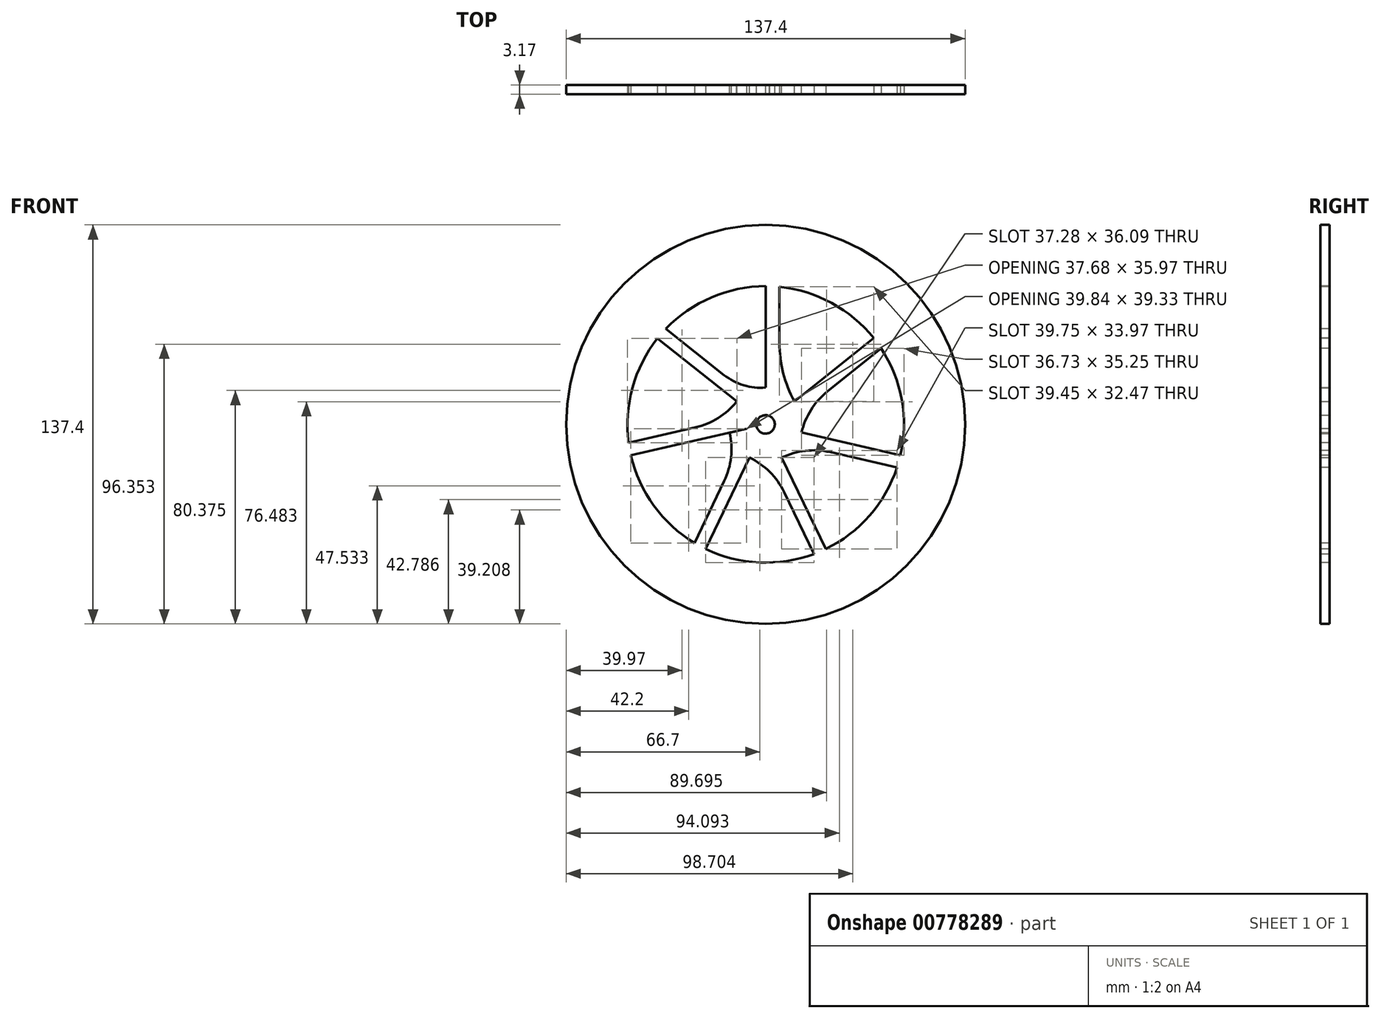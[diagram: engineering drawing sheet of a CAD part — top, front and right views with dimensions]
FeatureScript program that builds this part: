
annotation { "Feature Type Name" : "Feature", "Feature Type Description" : "" }
export const myFeature = defineFeature(function(context is Context, id is Id, definition is map)
    precondition{}
    {
        {
            var Q0;
            Q0=qCreatedBy(makeId("Front.planeOp"),FACE);
            var sketch = newSketch(context, id + "F0", { "sketchPlane" : qUnion([Q0])});
            skCircle(sketch, "E0", {"center": v(0, 0) * mm, "radius": 76.2 * mm, "construction": true});
            skCircle(sketch, "E1", {"center": v(0, 0) * mm, "radius": 68.7 * mm});
            skLineSegment(sketch, "E2", {"start": v(0, 0) * mm, "end": v(0, 105.2) * mm, "construction": true});
            skLineSegment(sketch, "E3", {"start": v(0.8, 92.24) * mm, "end": v(0.8, 62) * mm, "construction": true});
            skLineSegment(sketch, "E4", {"start": v(5.16, 61.23) * mm, "end": v(5.16, 89.94) * mm, "construction": true});
            skLineSegment(sketch, "E5", {"start": v(3.37, 89.43) * mm, "end": v(3.37, 60.2) * mm, "construction": true});
            skLineSegment(sketch, "E6", {"start": v(0, 69.1) * mm, "end": v(51.77, 69.1) * mm, "construction": true});
            skLineSegment(sketch, "E7", {"start": v(0, 76.2) * mm, "end": v(28.84, 76.2) * mm, "construction": true});
            skLineSegment(sketch, "E8", {"start": v(0, 76) * mm, "end": v(28.7, 76) * mm, "construction": true});
            skLineSegment(sketch, "E9", {"start": v(1, 77.75) * mm, "end": v(1, 72.49) * mm, "construction": true});
            skArc(sketch, "E10", {"start": v(3.37, 69.1) * mm, "mid": v(2.54, 72.68) * mm, "end": v(1, 76) * mm});
            skArc(sketch, "E11", {"start": v(3.37, 69.1) * mm, "mid": v(4.23, 68.69) * mm, "end": v(5.16, 68.51) * mm});
            skArc(sketch, "E12", {"start": v(1, 76) * mm, "mid": v(0.91, 76.1) * mm, "end": v(0.8, 76.14) * mm});
            skArc(sketch, "E13.MirrorCS", {"start": v(-3.37, 69.1) * mm, "mid": v(-2.54, 72.68) * mm, "end": v(-1, 76) * mm});
            skArc(sketch, "E14.MirrorCS", {"start": v(-3.37, 69.1) * mm, "mid": v(-4.23, 68.69) * mm, "end": v(-5.16, 68.51) * mm});
            skArc(sketch, "E15.MirrorCS", {"start": v(-1, 76) * mm, "mid": v(-0.91, 76.1) * mm, "end": v(-0.8, 76.14) * mm});
            skArc(sketch, "E16", {"start": v(0.8, 76.14) * mm, "mid": v(0, 76.2) * mm, "end": v(-0.8, 76.14) * mm});
            skSolve(sketch);
        }
        {
            var Q0;
            {var subQ1=sQuery(id+"F0.wireOp",EDGE,"E10");Q0=makeQuery(id+"F0.imprint","IMPRINT",FACE,{"disambiguationData":[TD([[makeQuery(id+"F0.imprint","IMPRINT",EDGE,{"derivedFrom":subQ1}),1.0]])]});}
            var Q1;
            {var subQ0=sQuery(id+"F0.wireOp",EDGE,"E11");var subQ1=sQuery(id+"F0.wireOp",EDGE,"E1");var subQ2=makeQuery(id+"F0.imprint","INTERSECT",VERTEX,{"disambiguationData":[OD(1.0)],"derivedFrom":[subQ1,subQ0]});Q1=makeQuery(id+"F0.imprint","IMPRINT",FACE,{"disambiguationData":[TD([[makeQuery(id+"F0.imprint","IMPRINT",EDGE,{"disambiguationData":[TD([[subQ2,-1.0]])],"derivedFrom":subQ1}),1.0]])]});}
            extrude(context, id + "F1", {"entities" : qUnion([Q0, Q1]), "depth" : 3.17 * mm, "offsetDistance" : 25.4 * mm});
        }
        {
            var Q0;
            Q0=makeQuery(id+"F1.opExtrude","SWEPT_BODY",BODY,{"disambiguationData":[OSD([sQuery(id+"F0.wireOp",EDGE,"E1"),sQuery(id+"F0.wireOp",EDGE,"E10"),sQuery(id+"F0.wireOp",EDGE,"E11"),sQuery(id+"F0.wireOp",EDGE,"E12"),sQuery(id+"F0.wireOp",EDGE,"E13.MirrorCS"),sQuery(id+"F0.wireOp",EDGE,"E14.MirrorCS"),sQuery(id+"F0.wireOp",EDGE,"E15.MirrorCS"),sQuery(id+"F0.wireOp",EDGE,"E16")])]});
            var Q1;
            Q1=makeQuery(id+"F1.opExtrude","SWEPT_FACE",FACE,{"disambiguationData":[OSD([sQuery(id+"F0.wireOp",EDGE,"E1")])]});
            circularPattern(context, id + "F2", {"operationType" : NewBodyOperationType.ADD, "entities" : qUnion([Q0]), "axis" : qUnion([Q1]), "angle" : 8.57 * degree, "instanceCount" : 42});
        }
        {
            var Q0;
            Q0=makeQuery(id+"F1.opExtrude","CAP_FACE",FACE,{"disambiguationData":[OSD([sQuery(id+"F0.wireOp",EDGE,"E1"),sQuery(id+"F0.wireOp",EDGE,"E10"),sQuery(id+"F0.wireOp",EDGE,"E11"),sQuery(id+"F0.wireOp",EDGE,"E12"),sQuery(id+"F0.wireOp",EDGE,"E13.MirrorCS"),sQuery(id+"F0.wireOp",EDGE,"E14.MirrorCS"),sQuery(id+"F0.wireOp",EDGE,"E15.MirrorCS"),sQuery(id+"F0.wireOp",EDGE,"E16")])],"isStart":false});
            var sketch = newSketch(context, id + "F3", { "sketchPlane" : qUnion([Q0])});
            skCircle(sketch, "E17", {"center": v(0, 0) * mm, "radius": 47.63 * mm, "construction": true});
            skLineSegment(sketch, "E18", {"start": v(0, 0) * mm, "end": v(0, 47.63) * mm, "construction": true});
            skLineSegment(sketch, "E19", {"start": v(0, 0) * mm, "end": v(37.23, 29.7) * mm, "construction": true});
            skLineSegment(sketch, "E20", {"start": v(0, 0) * mm, "end": v(46.43, -10.58) * mm, "construction": true});
            skLineSegment(sketch, "E21", {"start": v(0, 0) * mm, "end": v(20.68, -42.9) * mm, "construction": true});
            skLineSegment(sketch, "E22", {"start": v(0, 0) * mm, "end": v(-20.64, -42.92) * mm, "construction": true});
            skLineSegment(sketch, "E23", {"start": v(0, 0) * mm, "end": v(-46.42, -10.63) * mm, "construction": true});
            skLineSegment(sketch, "E24", {"start": v(0, 0) * mm, "end": v(-37.26, 29.66) * mm, "construction": true});
            skCircle(sketch, "E25", {"center": v(0, 0) * mm, "radius": 9.53 * mm, "construction": true});
            skLineSegment(sketch, "E26", {"start": v(3.17, 47.52) * mm, "end": v(3.18, 8.98) * mm, "construction": true});
            skLineSegment(sketch, "E27", {"start": v(39.13, 27.15) * mm, "end": v(9, 3.12) * mm, "construction": true});
            skLineSegment(sketch, "E28", {"start": v(45.63, -13.66) * mm, "end": v(8.05, -5.1) * mm, "construction": true});
            skLineSegment(sketch, "E29", {"start": v(1.04, -9.47) * mm, "end": v(17.78, -44.18) * mm, "construction": true});
            skLineSegment(sketch, "E30", {"start": v(-6.75, -6.72) * mm, "end": v(-23.45, -41.45) * mm, "construction": true});
            skLineSegment(sketch, "E31", {"start": v(-9.46, 1.1) * mm, "end": v(-47.03, -7.51) * mm, "construction": true});
            skLineSegment(sketch, "E32", {"start": v(-5.05, 8.08) * mm, "end": v(-35.2, 32.08) * mm, "construction": true});
            skCircle(sketch, "E33", {"center": v(0, 0) * mm, "radius": 25.4 * mm, "construction": true});
            skLineSegment(sketch, "E34", {"start": v(3.17, 47.52) * mm, "end": v(4.45, 9.15) * mm});
            skArc(sketch, "E35", {"start": v(4.45, 9.15) * mm, "mid": v(4.72, 6.68) * mm, "end": v(5.38, 4.3) * mm});
            skArc(sketch, "E36", {"start": v(37.23, 29.7) * mm, "mid": v(22.06, 42.16) * mm, "end": v(3.17, 47.52) * mm});
            skLineSegment(sketch, "E37", {"start": v(5.38, 4.3) * mm, "end": v(37.23, 29.7) * mm});
            skCircle(sketch, "E38", {"center": v(0, 0) * mm, "radius": 10.17 * mm, "construction": true});
            skLineSegment(sketch, "E39", {"start": v(9.93, 2.23) * mm, "end": v(39.13, 27.15) * mm});
            skArc(sketch, "E40", {"start": v(9.93, 2.23) * mm, "mid": v(8.17, 0.48) * mm, "end": v(6.7, -1.53) * mm});
            skArc(sketch, "E41", {"start": v(46.43, -10.58) * mm, "mid": v(46.78, 9.06) * mm, "end": v(39.13, 27.15) * mm});
            skLineSegment(sketch, "E42", {"start": v(6.7, -1.53) * mm, "end": v(46.43, -10.58) * mm});
            skLineSegment(sketch, "E43", {"start": v(7.93, -6.37) * mm, "end": v(45.63, -13.66) * mm});
            skArc(sketch, "E44", {"start": v(7.93, -6.37) * mm, "mid": v(5.47, -6.09) * mm, "end": v(2.99, -6.2) * mm});
            skArc(sketch, "E45", {"start": v(20.68, -42.9) * mm, "mid": v(36.25, -30.91) * mm, "end": v(45.63, -13.66) * mm});
            skLineSegment(sketch, "E46", {"start": v(2.99, -6.2) * mm, "end": v(20.68, -42.9) * mm});
            skLineSegment(sketch, "E47", {"start": v(-0.03, -10.17) * mm, "end": v(17.78, -44.18) * mm});
            skArc(sketch, "E48", {"start": v(-0.03, -10.17) * mm, "mid": v(-1.35, -8.07) * mm, "end": v(-2.98, -6.2) * mm});
            skArc(sketch, "E49", {"start": v(-20.64, -42.92) * mm, "mid": v(-1.56, -47.56) * mm, "end": v(17.78, -44.18) * mm});
            skLineSegment(sketch, "E50", {"start": v(-20.64, -42.92) * mm, "end": v(-2.98, -6.2) * mm});
            skLineSegment(sketch, "E51", {"start": v(-7.7, -6.65) * mm, "end": v(-23.45, -41.45) * mm});
            skArc(sketch, "E52", {"start": v(-7.7, -6.65) * mm, "mid": v(-6.87, -4.14) * mm, "end": v(-6.58, -1.5) * mm});
            skArc(sketch, "E53", {"start": v(-46.42, -10.63) * mm, "mid": v(-38.16, -28.44) * mm, "end": v(-23.45, -41.45) * mm});
            skLineSegment(sketch, "E54", {"start": v(-46.42, -10.63) * mm, "end": v(-6.58, -1.5) * mm});
            skArc(sketch, "E55", {"start": v(-8.44, 5.67) * mm, "mid": v(-8, 5.84) * mm, "end": v(-7.55, 6) * mm});
            skArc(sketch, "E56", {"start": v(-37.26, 29.66) * mm, "mid": v(-46, 12.09) * mm, "end": v(-47.03, -7.51) * mm});
            skLineSegment(sketch, "E57", {"start": v(-37.26, 29.66) * mm, "end": v(-7.55, 6) * mm});
            skLineSegment(sketch, "E58", {"start": v(-4.38, 9.18) * mm, "end": v(-35.2, 32.08) * mm});
            skArc(sketch, "E59", {"start": v(-4.38, 9.18) * mm, "mid": v(-2.28, 7.86) * mm, "end": v(0, 6.88) * mm});
            skArc(sketch, "E60", {"start": v(3.17, 47.52) * mm, "mid": v(-17.75, 44.12) * mm, "end": v(-35.2, 32.08) * mm});
            skLineSegment(sketch, "E61", {"start": v(0, 6.88) * mm, "end": v(0, 47.63) * mm});
            skCircle(sketch, "E62", {"center": v(-13.78, -21.34) * mm, "radius": 15.88 * mm, "construction": true});
            skArc(sketch, "E63", {"start": v(-10.12, 1.1) * mm, "mid": v(-7.38, 2.15) * mm, "end": v(-5.38, 4.29) * mm, "construction": true});
            skArc(sketch, "E64", {"start": v(-10.12, 1.1) * mm, "mid": v(-7.4, 2.16) * mm, "end": v(-5.38, 4.29) * mm});
            skLineSegment(sketch, "E65", {"start": v(-47.03, -7.51) * mm, "end": v(-10.12, 1.1) * mm});
            skLineSegment(sketch, "E66", {"start": v(-37.26, 29.66) * mm, "end": v(-5.38, 4.29) * mm});
            skSolve(sketch);
        }
        {
            var Q0;
            Q0=makeQuery(id+"F3.imprint","IMPRINT",FACE,{"disambiguationData":[TD([[makeQuery(id+"F3.imprint","IMPRINT",EDGE,{"derivedFrom":sQuery(id+"F3.wireOp",EDGE,"E39")}),-1.0]])]});
            var Q1;
            Q1=makeQuery(id+"F3.imprint","IMPRINT",FACE,{"disambiguationData":[TD([[makeQuery(id+"F3.imprint","IMPRINT",EDGE,{"derivedFrom":sQuery(id+"F3.wireOp",EDGE,"E34")}),1.0]])]});
            var Q2;
            {var subQ0=sQuery(id+"F3.wireOp",EDGE,"E58");Q2=makeQuery(id+"F3.imprint","IMPRINT",FACE,{"disambiguationData":[TD([[makeQuery(id+"F3.imprint","IMPRINT",EDGE,{"derivedFrom":subQ0}),-1.0]])]});}
            var Q3;
            Q3=makeQuery(id+"F3.imprint","IMPRINT",FACE,{"disambiguationData":[TD([[makeQuery(id+"F3.imprint","IMPRINT",EDGE,{"derivedFrom":sQuery(id+"F3.wireOp",EDGE,"F4JjJbdY-lvNh-I1ea-Elyr-KsVFTcUKGLhJ")}),1.0]])]});
            var Q4;
            Q4=makeQuery(id+"F3.imprint","IMPRINT",FACE,{"disambiguationData":[TD([[makeQuery(id+"F3.imprint","IMPRINT",EDGE,{"derivedFrom":sQuery(id+"F3.wireOp",EDGE,"E51")}),-1.0]])]});
            var Q5;
            Q5=makeQuery(id+"F3.imprint","IMPRINT",FACE,{"disambiguationData":[TD([[makeQuery(id+"F3.imprint","IMPRINT",EDGE,{"derivedFrom":sQuery(id+"F3.wireOp",EDGE,"E47")}),-1.0]])]});
            var Q6;
            Q6=makeQuery(id+"F3.imprint","IMPRINT",FACE,{"disambiguationData":[TD([[makeQuery(id+"F3.imprint","IMPRINT",EDGE,{"derivedFrom":sQuery(id+"F3.wireOp",EDGE,"E43")}),-1.0]])]});
            var Q7;
            {var subQ2=sQuery(id+"F3.wireOp",EDGE,"E56");Q7=makeQuery(id+"F3.imprint","IMPRINT",FACE,{"disambiguationData":[TD([[makeQuery(id+"F3.imprint","IMPRINT",EDGE,{"derivedFrom":subQ2}),1.0]])]});}
            extrude(context, id + "F4", {"entities" : qUnion([Q0, Q1, Q2, Q3, Q4, Q5, Q6, Q7]), "operationType" : NewBodyOperationType.REMOVE, "oppositeDirection" : true, "depth" : 25.4 * mm, "offsetDistance" : 25.4 * mm});
        }
        {
            var Q0;
            Q0=sQuery(id+"F0.wireOp",VERTEX,"E2.start");
            var Q1;
            Q1=makeQuery(id+"F1.opExtrude","SWEPT_BODY",BODY,{"disambiguationData":[OSD([sQuery(id+"F0.wireOp",EDGE,"E1"),sQuery(id+"F0.wireOp",EDGE,"E10"),sQuery(id+"F0.wireOp",EDGE,"E11"),sQuery(id+"F0.wireOp",EDGE,"E12"),sQuery(id+"F0.wireOp",EDGE,"E13.MirrorCS"),sQuery(id+"F0.wireOp",EDGE,"E14.MirrorCS"),sQuery(id+"F0.wireOp",EDGE,"E15.MirrorCS"),sQuery(id+"F0.wireOp",EDGE,"E16")])]});
            var Q2;
            Q2=makeQuery(id+"F2.opPattern","COPY",BODY,{"derivedFrom":makeQuery(id+"F1.opExtrude","SWEPT_BODY",BODY,{"disambiguationData":[OSD([sQuery(id+"F0.wireOp",EDGE,"E1"),sQuery(id+"F0.wireOp",EDGE,"E10"),sQuery(id+"F0.wireOp",EDGE,"E11"),sQuery(id+"F0.wireOp",EDGE,"E12"),sQuery(id+"F0.wireOp",EDGE,"E13.MirrorCS"),sQuery(id+"F0.wireOp",EDGE,"E14.MirrorCS"),sQuery(id+"F0.wireOp",EDGE,"E15.MirrorCS"),sQuery(id+"F0.wireOp",EDGE,"E16")])]}),"instanceName":"1"});
            var Q3;
            Q3=makeQuery(id+"F2.opPattern","COPY",BODY,{"derivedFrom":makeQuery(id+"F1.opExtrude","SWEPT_BODY",BODY,{"disambiguationData":[OSD([sQuery(id+"F0.wireOp",EDGE,"E1"),sQuery(id+"F0.wireOp",EDGE,"E10"),sQuery(id+"F0.wireOp",EDGE,"E11"),sQuery(id+"F0.wireOp",EDGE,"E12"),sQuery(id+"F0.wireOp",EDGE,"E13.MirrorCS"),sQuery(id+"F0.wireOp",EDGE,"E14.MirrorCS"),sQuery(id+"F0.wireOp",EDGE,"E15.MirrorCS"),sQuery(id+"F0.wireOp",EDGE,"E16")])]}),"instanceName":"2"});
            var Q4;
            Q4=makeQuery(id+"F2.opPattern","COPY",BODY,{"derivedFrom":makeQuery(id+"F1.opExtrude","SWEPT_BODY",BODY,{"disambiguationData":[OSD([sQuery(id+"F0.wireOp",EDGE,"E1"),sQuery(id+"F0.wireOp",EDGE,"E10"),sQuery(id+"F0.wireOp",EDGE,"E11"),sQuery(id+"F0.wireOp",EDGE,"E12"),sQuery(id+"F0.wireOp",EDGE,"E13.MirrorCS"),sQuery(id+"F0.wireOp",EDGE,"E14.MirrorCS"),sQuery(id+"F0.wireOp",EDGE,"E15.MirrorCS"),sQuery(id+"F0.wireOp",EDGE,"E16")])]}),"instanceName":"3"});
            var Q5;
            Q5=makeQuery(id+"F2.opPattern","COPY",BODY,{"derivedFrom":makeQuery(id+"F1.opExtrude","SWEPT_BODY",BODY,{"disambiguationData":[OSD([sQuery(id+"F0.wireOp",EDGE,"E1"),sQuery(id+"F0.wireOp",EDGE,"E10"),sQuery(id+"F0.wireOp",EDGE,"E11"),sQuery(id+"F0.wireOp",EDGE,"E12"),sQuery(id+"F0.wireOp",EDGE,"E13.MirrorCS"),sQuery(id+"F0.wireOp",EDGE,"E14.MirrorCS"),sQuery(id+"F0.wireOp",EDGE,"E15.MirrorCS"),sQuery(id+"F0.wireOp",EDGE,"E16")])]}),"instanceName":"4"});
            var Q6;
            Q6=makeQuery(id+"F2.opPattern","COPY",BODY,{"derivedFrom":makeQuery(id+"F1.opExtrude","SWEPT_BODY",BODY,{"disambiguationData":[OSD([sQuery(id+"F0.wireOp",EDGE,"E1"),sQuery(id+"F0.wireOp",EDGE,"E10"),sQuery(id+"F0.wireOp",EDGE,"E11"),sQuery(id+"F0.wireOp",EDGE,"E12"),sQuery(id+"F0.wireOp",EDGE,"E13.MirrorCS"),sQuery(id+"F0.wireOp",EDGE,"E14.MirrorCS"),sQuery(id+"F0.wireOp",EDGE,"E15.MirrorCS"),sQuery(id+"F0.wireOp",EDGE,"E16")])]}),"instanceName":"5"});
            var Q7;
            Q7=makeQuery(id+"F2.opPattern","COPY",BODY,{"derivedFrom":makeQuery(id+"F1.opExtrude","SWEPT_BODY",BODY,{"disambiguationData":[OSD([sQuery(id+"F0.wireOp",EDGE,"E1"),sQuery(id+"F0.wireOp",EDGE,"E10"),sQuery(id+"F0.wireOp",EDGE,"E11"),sQuery(id+"F0.wireOp",EDGE,"E12"),sQuery(id+"F0.wireOp",EDGE,"E13.MirrorCS"),sQuery(id+"F0.wireOp",EDGE,"E14.MirrorCS"),sQuery(id+"F0.wireOp",EDGE,"E15.MirrorCS"),sQuery(id+"F0.wireOp",EDGE,"E16")])]}),"instanceName":"6"});
            var Q8;
            Q8=makeQuery(id+"F2.opPattern","COPY",BODY,{"derivedFrom":makeQuery(id+"F1.opExtrude","SWEPT_BODY",BODY,{"disambiguationData":[OSD([sQuery(id+"F0.wireOp",EDGE,"E1"),sQuery(id+"F0.wireOp",EDGE,"E10"),sQuery(id+"F0.wireOp",EDGE,"E11"),sQuery(id+"F0.wireOp",EDGE,"E12"),sQuery(id+"F0.wireOp",EDGE,"E13.MirrorCS"),sQuery(id+"F0.wireOp",EDGE,"E14.MirrorCS"),sQuery(id+"F0.wireOp",EDGE,"E15.MirrorCS"),sQuery(id+"F0.wireOp",EDGE,"E16")])]}),"instanceName":"7"});
            var Q9;
            Q9=makeQuery(id+"F2.opPattern","COPY",BODY,{"derivedFrom":makeQuery(id+"F1.opExtrude","SWEPT_BODY",BODY,{"disambiguationData":[OSD([sQuery(id+"F0.wireOp",EDGE,"E1"),sQuery(id+"F0.wireOp",EDGE,"E10"),sQuery(id+"F0.wireOp",EDGE,"E11"),sQuery(id+"F0.wireOp",EDGE,"E12"),sQuery(id+"F0.wireOp",EDGE,"E13.MirrorCS"),sQuery(id+"F0.wireOp",EDGE,"E14.MirrorCS"),sQuery(id+"F0.wireOp",EDGE,"E15.MirrorCS"),sQuery(id+"F0.wireOp",EDGE,"E16")])]}),"instanceName":"8"});
            var Q10;
            Q10=makeQuery(id+"F2.opPattern","COPY",BODY,{"derivedFrom":makeQuery(id+"F1.opExtrude","SWEPT_BODY",BODY,{"disambiguationData":[OSD([sQuery(id+"F0.wireOp",EDGE,"E1"),sQuery(id+"F0.wireOp",EDGE,"E10"),sQuery(id+"F0.wireOp",EDGE,"E11"),sQuery(id+"F0.wireOp",EDGE,"E12"),sQuery(id+"F0.wireOp",EDGE,"E13.MirrorCS"),sQuery(id+"F0.wireOp",EDGE,"E14.MirrorCS"),sQuery(id+"F0.wireOp",EDGE,"E15.MirrorCS"),sQuery(id+"F0.wireOp",EDGE,"E16")])]}),"instanceName":"9"});
            var Q11;
            Q11=makeQuery(id+"F2.opPattern","COPY",BODY,{"derivedFrom":makeQuery(id+"F1.opExtrude","SWEPT_BODY",BODY,{"disambiguationData":[OSD([sQuery(id+"F0.wireOp",EDGE,"E1"),sQuery(id+"F0.wireOp",EDGE,"E10"),sQuery(id+"F0.wireOp",EDGE,"E11"),sQuery(id+"F0.wireOp",EDGE,"E12"),sQuery(id+"F0.wireOp",EDGE,"E13.MirrorCS"),sQuery(id+"F0.wireOp",EDGE,"E14.MirrorCS"),sQuery(id+"F0.wireOp",EDGE,"E15.MirrorCS"),sQuery(id+"F0.wireOp",EDGE,"E16")])]}),"instanceName":"10"});
            var Q12;
            Q12=makeQuery(id+"F2.opPattern","COPY",BODY,{"derivedFrom":makeQuery(id+"F1.opExtrude","SWEPT_BODY",BODY,{"disambiguationData":[OSD([sQuery(id+"F0.wireOp",EDGE,"E1"),sQuery(id+"F0.wireOp",EDGE,"E10"),sQuery(id+"F0.wireOp",EDGE,"E11"),sQuery(id+"F0.wireOp",EDGE,"E12"),sQuery(id+"F0.wireOp",EDGE,"E13.MirrorCS"),sQuery(id+"F0.wireOp",EDGE,"E14.MirrorCS"),sQuery(id+"F0.wireOp",EDGE,"E15.MirrorCS"),sQuery(id+"F0.wireOp",EDGE,"E16")])]}),"instanceName":"11"});
            var Q13;
            Q13=makeQuery(id+"F2.opPattern","COPY",BODY,{"derivedFrom":makeQuery(id+"F1.opExtrude","SWEPT_BODY",BODY,{"disambiguationData":[OSD([sQuery(id+"F0.wireOp",EDGE,"E1"),sQuery(id+"F0.wireOp",EDGE,"E10"),sQuery(id+"F0.wireOp",EDGE,"E11"),sQuery(id+"F0.wireOp",EDGE,"E12"),sQuery(id+"F0.wireOp",EDGE,"E13.MirrorCS"),sQuery(id+"F0.wireOp",EDGE,"E14.MirrorCS"),sQuery(id+"F0.wireOp",EDGE,"E15.MirrorCS"),sQuery(id+"F0.wireOp",EDGE,"E16")])]}),"instanceName":"12"});
            var Q14;
            Q14=makeQuery(id+"F2.opPattern","COPY",BODY,{"derivedFrom":makeQuery(id+"F1.opExtrude","SWEPT_BODY",BODY,{"disambiguationData":[OSD([sQuery(id+"F0.wireOp",EDGE,"E1"),sQuery(id+"F0.wireOp",EDGE,"E10"),sQuery(id+"F0.wireOp",EDGE,"E11"),sQuery(id+"F0.wireOp",EDGE,"E12"),sQuery(id+"F0.wireOp",EDGE,"E13.MirrorCS"),sQuery(id+"F0.wireOp",EDGE,"E14.MirrorCS"),sQuery(id+"F0.wireOp",EDGE,"E15.MirrorCS"),sQuery(id+"F0.wireOp",EDGE,"E16")])]}),"instanceName":"13"});
            var Q15;
            Q15=makeQuery(id+"F2.opPattern","COPY",BODY,{"derivedFrom":makeQuery(id+"F1.opExtrude","SWEPT_BODY",BODY,{"disambiguationData":[OSD([sQuery(id+"F0.wireOp",EDGE,"E1"),sQuery(id+"F0.wireOp",EDGE,"E10"),sQuery(id+"F0.wireOp",EDGE,"E11"),sQuery(id+"F0.wireOp",EDGE,"E12"),sQuery(id+"F0.wireOp",EDGE,"E13.MirrorCS"),sQuery(id+"F0.wireOp",EDGE,"E14.MirrorCS"),sQuery(id+"F0.wireOp",EDGE,"E15.MirrorCS"),sQuery(id+"F0.wireOp",EDGE,"E16")])]}),"instanceName":"14"});
            var Q16;
            Q16=makeQuery(id+"F2.opPattern","COPY",BODY,{"derivedFrom":makeQuery(id+"F1.opExtrude","SWEPT_BODY",BODY,{"disambiguationData":[OSD([sQuery(id+"F0.wireOp",EDGE,"E1"),sQuery(id+"F0.wireOp",EDGE,"E10"),sQuery(id+"F0.wireOp",EDGE,"E11"),sQuery(id+"F0.wireOp",EDGE,"E12"),sQuery(id+"F0.wireOp",EDGE,"E13.MirrorCS"),sQuery(id+"F0.wireOp",EDGE,"E14.MirrorCS"),sQuery(id+"F0.wireOp",EDGE,"E15.MirrorCS"),sQuery(id+"F0.wireOp",EDGE,"E16")])]}),"instanceName":"15"});
            var Q17;
            Q17=makeQuery(id+"F2.opPattern","COPY",BODY,{"derivedFrom":makeQuery(id+"F1.opExtrude","SWEPT_BODY",BODY,{"disambiguationData":[OSD([sQuery(id+"F0.wireOp",EDGE,"E1"),sQuery(id+"F0.wireOp",EDGE,"E10"),sQuery(id+"F0.wireOp",EDGE,"E11"),sQuery(id+"F0.wireOp",EDGE,"E12"),sQuery(id+"F0.wireOp",EDGE,"E13.MirrorCS"),sQuery(id+"F0.wireOp",EDGE,"E14.MirrorCS"),sQuery(id+"F0.wireOp",EDGE,"E15.MirrorCS"),sQuery(id+"F0.wireOp",EDGE,"E16")])]}),"instanceName":"16"});
            var Q18;
            Q18=makeQuery(id+"F2.opPattern","COPY",BODY,{"derivedFrom":makeQuery(id+"F1.opExtrude","SWEPT_BODY",BODY,{"disambiguationData":[OSD([sQuery(id+"F0.wireOp",EDGE,"E1"),sQuery(id+"F0.wireOp",EDGE,"E10"),sQuery(id+"F0.wireOp",EDGE,"E11"),sQuery(id+"F0.wireOp",EDGE,"E12"),sQuery(id+"F0.wireOp",EDGE,"E13.MirrorCS"),sQuery(id+"F0.wireOp",EDGE,"E14.MirrorCS"),sQuery(id+"F0.wireOp",EDGE,"E15.MirrorCS"),sQuery(id+"F0.wireOp",EDGE,"E16")])]}),"instanceName":"17"});
            var Q19;
            Q19=makeQuery(id+"F2.opPattern","COPY",BODY,{"derivedFrom":makeQuery(id+"F1.opExtrude","SWEPT_BODY",BODY,{"disambiguationData":[OSD([sQuery(id+"F0.wireOp",EDGE,"E1"),sQuery(id+"F0.wireOp",EDGE,"E10"),sQuery(id+"F0.wireOp",EDGE,"E11"),sQuery(id+"F0.wireOp",EDGE,"E12"),sQuery(id+"F0.wireOp",EDGE,"E13.MirrorCS"),sQuery(id+"F0.wireOp",EDGE,"E14.MirrorCS"),sQuery(id+"F0.wireOp",EDGE,"E15.MirrorCS"),sQuery(id+"F0.wireOp",EDGE,"E16")])]}),"instanceName":"18"});
            var Q20;
            Q20=makeQuery(id+"F2.opPattern","COPY",BODY,{"derivedFrom":makeQuery(id+"F1.opExtrude","SWEPT_BODY",BODY,{"disambiguationData":[OSD([sQuery(id+"F0.wireOp",EDGE,"E1"),sQuery(id+"F0.wireOp",EDGE,"E10"),sQuery(id+"F0.wireOp",EDGE,"E11"),sQuery(id+"F0.wireOp",EDGE,"E12"),sQuery(id+"F0.wireOp",EDGE,"E13.MirrorCS"),sQuery(id+"F0.wireOp",EDGE,"E14.MirrorCS"),sQuery(id+"F0.wireOp",EDGE,"E15.MirrorCS"),sQuery(id+"F0.wireOp",EDGE,"E16")])]}),"instanceName":"19"});
            var Q21;
            Q21=makeQuery(id+"F2.opPattern","COPY",BODY,{"derivedFrom":makeQuery(id+"F1.opExtrude","SWEPT_BODY",BODY,{"disambiguationData":[OSD([sQuery(id+"F0.wireOp",EDGE,"E1"),sQuery(id+"F0.wireOp",EDGE,"E10"),sQuery(id+"F0.wireOp",EDGE,"E11"),sQuery(id+"F0.wireOp",EDGE,"E12"),sQuery(id+"F0.wireOp",EDGE,"E13.MirrorCS"),sQuery(id+"F0.wireOp",EDGE,"E14.MirrorCS"),sQuery(id+"F0.wireOp",EDGE,"E15.MirrorCS"),sQuery(id+"F0.wireOp",EDGE,"E16")])]}),"instanceName":"20"});
            var Q22;
            Q22=makeQuery(id+"F2.opPattern","COPY",BODY,{"derivedFrom":makeQuery(id+"F1.opExtrude","SWEPT_BODY",BODY,{"disambiguationData":[OSD([sQuery(id+"F0.wireOp",EDGE,"E1"),sQuery(id+"F0.wireOp",EDGE,"E10"),sQuery(id+"F0.wireOp",EDGE,"E11"),sQuery(id+"F0.wireOp",EDGE,"E12"),sQuery(id+"F0.wireOp",EDGE,"E13.MirrorCS"),sQuery(id+"F0.wireOp",EDGE,"E14.MirrorCS"),sQuery(id+"F0.wireOp",EDGE,"E15.MirrorCS"),sQuery(id+"F0.wireOp",EDGE,"E16")])]}),"instanceName":"21"});
            var Q23;
            Q23=makeQuery(id+"F2.opPattern","COPY",BODY,{"derivedFrom":makeQuery(id+"F1.opExtrude","SWEPT_BODY",BODY,{"disambiguationData":[OSD([sQuery(id+"F0.wireOp",EDGE,"E1"),sQuery(id+"F0.wireOp",EDGE,"E10"),sQuery(id+"F0.wireOp",EDGE,"E11"),sQuery(id+"F0.wireOp",EDGE,"E12"),sQuery(id+"F0.wireOp",EDGE,"E13.MirrorCS"),sQuery(id+"F0.wireOp",EDGE,"E14.MirrorCS"),sQuery(id+"F0.wireOp",EDGE,"E15.MirrorCS"),sQuery(id+"F0.wireOp",EDGE,"E16")])]}),"instanceName":"22"});
            var Q24;
            Q24=makeQuery(id+"F2.opPattern","COPY",BODY,{"derivedFrom":makeQuery(id+"F1.opExtrude","SWEPT_BODY",BODY,{"disambiguationData":[OSD([sQuery(id+"F0.wireOp",EDGE,"E1"),sQuery(id+"F0.wireOp",EDGE,"E10"),sQuery(id+"F0.wireOp",EDGE,"E11"),sQuery(id+"F0.wireOp",EDGE,"E12"),sQuery(id+"F0.wireOp",EDGE,"E13.MirrorCS"),sQuery(id+"F0.wireOp",EDGE,"E14.MirrorCS"),sQuery(id+"F0.wireOp",EDGE,"E15.MirrorCS"),sQuery(id+"F0.wireOp",EDGE,"E16")])]}),"instanceName":"23"});
            var Q25;
            Q25=makeQuery(id+"F2.opPattern","COPY",BODY,{"derivedFrom":makeQuery(id+"F1.opExtrude","SWEPT_BODY",BODY,{"disambiguationData":[OSD([sQuery(id+"F0.wireOp",EDGE,"E1"),sQuery(id+"F0.wireOp",EDGE,"E10"),sQuery(id+"F0.wireOp",EDGE,"E11"),sQuery(id+"F0.wireOp",EDGE,"E12"),sQuery(id+"F0.wireOp",EDGE,"E13.MirrorCS"),sQuery(id+"F0.wireOp",EDGE,"E14.MirrorCS"),sQuery(id+"F0.wireOp",EDGE,"E15.MirrorCS"),sQuery(id+"F0.wireOp",EDGE,"E16")])]}),"instanceName":"24"});
            var Q26;
            Q26=makeQuery(id+"F2.opPattern","COPY",BODY,{"derivedFrom":makeQuery(id+"F1.opExtrude","SWEPT_BODY",BODY,{"disambiguationData":[OSD([sQuery(id+"F0.wireOp",EDGE,"E1"),sQuery(id+"F0.wireOp",EDGE,"E10"),sQuery(id+"F0.wireOp",EDGE,"E11"),sQuery(id+"F0.wireOp",EDGE,"E12"),sQuery(id+"F0.wireOp",EDGE,"E13.MirrorCS"),sQuery(id+"F0.wireOp",EDGE,"E14.MirrorCS"),sQuery(id+"F0.wireOp",EDGE,"E15.MirrorCS"),sQuery(id+"F0.wireOp",EDGE,"E16")])]}),"instanceName":"25"});
            var Q27;
            Q27=makeQuery(id+"F2.opPattern","COPY",BODY,{"derivedFrom":makeQuery(id+"F1.opExtrude","SWEPT_BODY",BODY,{"disambiguationData":[OSD([sQuery(id+"F0.wireOp",EDGE,"E1"),sQuery(id+"F0.wireOp",EDGE,"E10"),sQuery(id+"F0.wireOp",EDGE,"E11"),sQuery(id+"F0.wireOp",EDGE,"E12"),sQuery(id+"F0.wireOp",EDGE,"E13.MirrorCS"),sQuery(id+"F0.wireOp",EDGE,"E14.MirrorCS"),sQuery(id+"F0.wireOp",EDGE,"E15.MirrorCS"),sQuery(id+"F0.wireOp",EDGE,"E16")])]}),"instanceName":"26"});
            var Q28;
            Q28=makeQuery(id+"F2.opPattern","COPY",BODY,{"derivedFrom":makeQuery(id+"F1.opExtrude","SWEPT_BODY",BODY,{"disambiguationData":[OSD([sQuery(id+"F0.wireOp",EDGE,"E1"),sQuery(id+"F0.wireOp",EDGE,"E10"),sQuery(id+"F0.wireOp",EDGE,"E11"),sQuery(id+"F0.wireOp",EDGE,"E12"),sQuery(id+"F0.wireOp",EDGE,"E13.MirrorCS"),sQuery(id+"F0.wireOp",EDGE,"E14.MirrorCS"),sQuery(id+"F0.wireOp",EDGE,"E15.MirrorCS"),sQuery(id+"F0.wireOp",EDGE,"E16")])]}),"instanceName":"27"});
            var Q29;
            Q29=makeQuery(id+"F2.opPattern","COPY",BODY,{"derivedFrom":makeQuery(id+"F1.opExtrude","SWEPT_BODY",BODY,{"disambiguationData":[OSD([sQuery(id+"F0.wireOp",EDGE,"E1"),sQuery(id+"F0.wireOp",EDGE,"E10"),sQuery(id+"F0.wireOp",EDGE,"E11"),sQuery(id+"F0.wireOp",EDGE,"E12"),sQuery(id+"F0.wireOp",EDGE,"E13.MirrorCS"),sQuery(id+"F0.wireOp",EDGE,"E14.MirrorCS"),sQuery(id+"F0.wireOp",EDGE,"E15.MirrorCS"),sQuery(id+"F0.wireOp",EDGE,"E16")])]}),"instanceName":"28"});
            var Q30;
            Q30=makeQuery(id+"F2.opPattern","COPY",BODY,{"derivedFrom":makeQuery(id+"F1.opExtrude","SWEPT_BODY",BODY,{"disambiguationData":[OSD([sQuery(id+"F0.wireOp",EDGE,"E1"),sQuery(id+"F0.wireOp",EDGE,"E10"),sQuery(id+"F0.wireOp",EDGE,"E11"),sQuery(id+"F0.wireOp",EDGE,"E12"),sQuery(id+"F0.wireOp",EDGE,"E13.MirrorCS"),sQuery(id+"F0.wireOp",EDGE,"E14.MirrorCS"),sQuery(id+"F0.wireOp",EDGE,"E15.MirrorCS"),sQuery(id+"F0.wireOp",EDGE,"E16")])]}),"instanceName":"29"});
            var Q31;
            Q31=makeQuery(id+"F2.opPattern","COPY",BODY,{"derivedFrom":makeQuery(id+"F1.opExtrude","SWEPT_BODY",BODY,{"disambiguationData":[OSD([sQuery(id+"F0.wireOp",EDGE,"E1"),sQuery(id+"F0.wireOp",EDGE,"E10"),sQuery(id+"F0.wireOp",EDGE,"E11"),sQuery(id+"F0.wireOp",EDGE,"E12"),sQuery(id+"F0.wireOp",EDGE,"E13.MirrorCS"),sQuery(id+"F0.wireOp",EDGE,"E14.MirrorCS"),sQuery(id+"F0.wireOp",EDGE,"E15.MirrorCS"),sQuery(id+"F0.wireOp",EDGE,"E16")])]}),"instanceName":"30"});
            var Q32;
            Q32=makeQuery(id+"F2.opPattern","COPY",BODY,{"derivedFrom":makeQuery(id+"F1.opExtrude","SWEPT_BODY",BODY,{"disambiguationData":[OSD([sQuery(id+"F0.wireOp",EDGE,"E1"),sQuery(id+"F0.wireOp",EDGE,"E10"),sQuery(id+"F0.wireOp",EDGE,"E11"),sQuery(id+"F0.wireOp",EDGE,"E12"),sQuery(id+"F0.wireOp",EDGE,"E13.MirrorCS"),sQuery(id+"F0.wireOp",EDGE,"E14.MirrorCS"),sQuery(id+"F0.wireOp",EDGE,"E15.MirrorCS"),sQuery(id+"F0.wireOp",EDGE,"E16")])]}),"instanceName":"31"});
            var Q33;
            Q33=makeQuery(id+"F2.opPattern","COPY",BODY,{"derivedFrom":makeQuery(id+"F1.opExtrude","SWEPT_BODY",BODY,{"disambiguationData":[OSD([sQuery(id+"F0.wireOp",EDGE,"E1"),sQuery(id+"F0.wireOp",EDGE,"E10"),sQuery(id+"F0.wireOp",EDGE,"E11"),sQuery(id+"F0.wireOp",EDGE,"E12"),sQuery(id+"F0.wireOp",EDGE,"E13.MirrorCS"),sQuery(id+"F0.wireOp",EDGE,"E14.MirrorCS"),sQuery(id+"F0.wireOp",EDGE,"E15.MirrorCS"),sQuery(id+"F0.wireOp",EDGE,"E16")])]}),"instanceName":"32"});
            var Q34;
            Q34=makeQuery(id+"F2.opPattern","COPY",BODY,{"derivedFrom":makeQuery(id+"F1.opExtrude","SWEPT_BODY",BODY,{"disambiguationData":[OSD([sQuery(id+"F0.wireOp",EDGE,"E1"),sQuery(id+"F0.wireOp",EDGE,"E10"),sQuery(id+"F0.wireOp",EDGE,"E11"),sQuery(id+"F0.wireOp",EDGE,"E12"),sQuery(id+"F0.wireOp",EDGE,"E13.MirrorCS"),sQuery(id+"F0.wireOp",EDGE,"E14.MirrorCS"),sQuery(id+"F0.wireOp",EDGE,"E15.MirrorCS"),sQuery(id+"F0.wireOp",EDGE,"E16")])]}),"instanceName":"33"});
            var Q35;
            Q35=makeQuery(id+"F2.opPattern","COPY",BODY,{"derivedFrom":makeQuery(id+"F1.opExtrude","SWEPT_BODY",BODY,{"disambiguationData":[OSD([sQuery(id+"F0.wireOp",EDGE,"E1"),sQuery(id+"F0.wireOp",EDGE,"E10"),sQuery(id+"F0.wireOp",EDGE,"E11"),sQuery(id+"F0.wireOp",EDGE,"E12"),sQuery(id+"F0.wireOp",EDGE,"E13.MirrorCS"),sQuery(id+"F0.wireOp",EDGE,"E14.MirrorCS"),sQuery(id+"F0.wireOp",EDGE,"E15.MirrorCS"),sQuery(id+"F0.wireOp",EDGE,"E16")])]}),"instanceName":"34"});
            var Q36;
            Q36=makeQuery(id+"F2.opPattern","COPY",BODY,{"derivedFrom":makeQuery(id+"F1.opExtrude","SWEPT_BODY",BODY,{"disambiguationData":[OSD([sQuery(id+"F0.wireOp",EDGE,"E1"),sQuery(id+"F0.wireOp",EDGE,"E10"),sQuery(id+"F0.wireOp",EDGE,"E11"),sQuery(id+"F0.wireOp",EDGE,"E12"),sQuery(id+"F0.wireOp",EDGE,"E13.MirrorCS"),sQuery(id+"F0.wireOp",EDGE,"E14.MirrorCS"),sQuery(id+"F0.wireOp",EDGE,"E15.MirrorCS"),sQuery(id+"F0.wireOp",EDGE,"E16")])]}),"instanceName":"35"});
            var Q37;
            Q37=makeQuery(id+"F2.opPattern","COPY",BODY,{"derivedFrom":makeQuery(id+"F1.opExtrude","SWEPT_BODY",BODY,{"disambiguationData":[OSD([sQuery(id+"F0.wireOp",EDGE,"E1"),sQuery(id+"F0.wireOp",EDGE,"E10"),sQuery(id+"F0.wireOp",EDGE,"E11"),sQuery(id+"F0.wireOp",EDGE,"E12"),sQuery(id+"F0.wireOp",EDGE,"E13.MirrorCS"),sQuery(id+"F0.wireOp",EDGE,"E14.MirrorCS"),sQuery(id+"F0.wireOp",EDGE,"E15.MirrorCS"),sQuery(id+"F0.wireOp",EDGE,"E16")])]}),"instanceName":"36"});
            var Q38;
            Q38=makeQuery(id+"F2.opPattern","COPY",BODY,{"derivedFrom":makeQuery(id+"F1.opExtrude","SWEPT_BODY",BODY,{"disambiguationData":[OSD([sQuery(id+"F0.wireOp",EDGE,"E1"),sQuery(id+"F0.wireOp",EDGE,"E10"),sQuery(id+"F0.wireOp",EDGE,"E11"),sQuery(id+"F0.wireOp",EDGE,"E12"),sQuery(id+"F0.wireOp",EDGE,"E13.MirrorCS"),sQuery(id+"F0.wireOp",EDGE,"E14.MirrorCS"),sQuery(id+"F0.wireOp",EDGE,"E15.MirrorCS"),sQuery(id+"F0.wireOp",EDGE,"E16")])]}),"instanceName":"37"});
            var Q39;
            Q39=makeQuery(id+"F2.opPattern","COPY",BODY,{"derivedFrom":makeQuery(id+"F1.opExtrude","SWEPT_BODY",BODY,{"disambiguationData":[OSD([sQuery(id+"F0.wireOp",EDGE,"E1"),sQuery(id+"F0.wireOp",EDGE,"E10"),sQuery(id+"F0.wireOp",EDGE,"E11"),sQuery(id+"F0.wireOp",EDGE,"E12"),sQuery(id+"F0.wireOp",EDGE,"E13.MirrorCS"),sQuery(id+"F0.wireOp",EDGE,"E14.MirrorCS"),sQuery(id+"F0.wireOp",EDGE,"E15.MirrorCS"),sQuery(id+"F0.wireOp",EDGE,"E16")])]}),"instanceName":"38"});
            var Q40;
            Q40=makeQuery(id+"F2.opPattern","COPY",BODY,{"derivedFrom":makeQuery(id+"F1.opExtrude","SWEPT_BODY",BODY,{"disambiguationData":[OSD([sQuery(id+"F0.wireOp",EDGE,"E1"),sQuery(id+"F0.wireOp",EDGE,"E10"),sQuery(id+"F0.wireOp",EDGE,"E11"),sQuery(id+"F0.wireOp",EDGE,"E12"),sQuery(id+"F0.wireOp",EDGE,"E13.MirrorCS"),sQuery(id+"F0.wireOp",EDGE,"E14.MirrorCS"),sQuery(id+"F0.wireOp",EDGE,"E15.MirrorCS"),sQuery(id+"F0.wireOp",EDGE,"E16")])]}),"instanceName":"39"});
            var Q41;
            Q41=makeQuery(id+"F2.opPattern","COPY",BODY,{"derivedFrom":makeQuery(id+"F1.opExtrude","SWEPT_BODY",BODY,{"disambiguationData":[OSD([sQuery(id+"F0.wireOp",EDGE,"E1"),sQuery(id+"F0.wireOp",EDGE,"E10"),sQuery(id+"F0.wireOp",EDGE,"E11"),sQuery(id+"F0.wireOp",EDGE,"E12"),sQuery(id+"F0.wireOp",EDGE,"E13.MirrorCS"),sQuery(id+"F0.wireOp",EDGE,"E14.MirrorCS"),sQuery(id+"F0.wireOp",EDGE,"E15.MirrorCS"),sQuery(id+"F0.wireOp",EDGE,"E16")])]}),"instanceName":"40"});
            var Q42;
            Q42=makeQuery(id+"F2.opPattern","COPY",BODY,{"derivedFrom":makeQuery(id+"F1.opExtrude","SWEPT_BODY",BODY,{"disambiguationData":[OSD([sQuery(id+"F0.wireOp",EDGE,"E1"),sQuery(id+"F0.wireOp",EDGE,"E10"),sQuery(id+"F0.wireOp",EDGE,"E11"),sQuery(id+"F0.wireOp",EDGE,"E12"),sQuery(id+"F0.wireOp",EDGE,"E13.MirrorCS"),sQuery(id+"F0.wireOp",EDGE,"E14.MirrorCS"),sQuery(id+"F0.wireOp",EDGE,"E15.MirrorCS"),sQuery(id+"F0.wireOp",EDGE,"E16")])]}),"instanceName":"41"});
            hole(context, id + "F5", {"style" : HoleStyle.SIMPLE, "endStyle" : HoleEndStyle.THROUGH, "oppositeDirection" : true, "holeDiameter" : 6.35 * mm, "majorDiameter" : 6.35 * mm, "isTappedThrough" : true, "tappedDepth" : 12.7 * mm, "tapClearance" : 3, "locations" : qUnion([Q0]), "scope" : qUnion([Q1, Q2, Q3, Q4, Q5, Q6, Q7, Q8, Q9, Q10, Q11, Q12, Q13, Q14, Q15, Q16, Q17, Q18, Q19, Q20, Q21, Q22, Q23, Q24, Q25, Q26, Q27, Q28, Q29, Q30, Q31, Q32, Q33, Q34, Q35, Q36, Q37, Q38, Q39, Q40, Q41, Q42])});
        }
        {
            var Q0;
            Q0=qCreatedBy(makeId("Front.planeOp"),FACE);
            var sketch = newSketch(context, id + "F6", { "sketchPlane" : qUnion([Q0])});
            skCircle(sketch, "E67", {"center": v(0, 0) * mm, "radius": 223.14 * mm, "construction": true});
            skLineSegment(sketch, "E68", {"start": v(0, 0) * mm, "end": v(0, 223.14) * mm, "construction": true});
            skCircle(sketch, "E69", {"center": v(0, 0) * mm, "radius": 12.7 * mm, "construction": true});
            skCircle(sketch, "E70", {"center": v(0, 0) * mm, "radius": 9.53 * mm, "construction": true});
            skCircle(sketch, "E71", {"center": v(0, 0) * mm, "radius": 47.67 * mm, "construction": true});
            skCircle(sketch, "E72", {"center": v(0, 0) * mm, "radius": 68.86 * mm, "construction": true});
            skLineSegment(sketch, "E73", {"start": v(4.76, 68.7) * mm, "end": v(4.76, 11.77) * mm, "construction": true});
            skCircle(sketch, "E74", {"center": v(0, 0) * mm, "radius": 38.1 * mm, "construction": true});
            skLineSegment(sketch, "E75", {"start": v(0, 0) * mm, "end": v(53.83, 42.94) * mm, "construction": true});
            skCircle(sketch, "E76", {"center": v(29.78, 23.76) * mm, "radius": 25.4 * mm, "construction": true});
            skLineSegment(sketch, "E77", {"start": v(4.76, 47.43) * mm, "end": v(4.76, 28.13) * mm});
            skArc(sketch, "E78", {"start": v(4.76, 28.13) * mm, "mid": v(6.07, 17.7) * mm, "end": v(9.93, 7.92) * mm});
            skLineSegment(sketch, "E79", {"start": v(9.93, 7.92) * mm, "end": v(4, 3.18) * mm});
            skLineSegment(sketch, "E80", {"start": v(4, 3.18) * mm, "end": v(3.09, 47.57) * mm});
            skLineSegment(sketch, "E81", {"start": v(3.09, 47.57) * mm, "end": v(4.76, 47.43) * mm});
            skLineSegment(sketch, "E82", {"start": v(0, 0) * mm, "end": v(80.94, -18.45) * mm, "construction": true});
            skLineSegment(sketch, "E83", {"start": v(0, 0) * mm, "end": v(35.5, -73.63) * mm, "construction": true});
            skLineSegment(sketch, "E84", {"start": v(0, 0) * mm, "end": v(-34.03, -70.77) * mm, "construction": true});
            skLineSegment(sketch, "E85", {"start": v(0, 0) * mm, "end": v(-80.55, -18.45) * mm, "construction": true});
            skLineSegment(sketch, "E86", {"start": v(-80.55, -18.45) * mm, "end": v(-80.55, -19.32) * mm, "construction": true});
            skLineSegment(sketch, "E87", {"start": v(0, 0) * mm, "end": v(-63.95, 50.9) * mm, "construction": true});
            skCircle(sketch, "E88", {"center": v(37.15, -8.47) * mm, "radius": 25.4 * mm, "construction": true});
            skCircle(sketch, "E89", {"center": v(16.55, -34.32) * mm, "radius": 25.4 * mm, "construction": true});
            skCircle(sketch, "E90", {"center": v(-16.51, -34.34) * mm, "radius": 25.4 * mm, "construction": true});
            skCircle(sketch, "E91", {"center": v(-37.14, -8.5) * mm, "radius": 25.4 * mm, "construction": true});
            skCircle(sketch, "E92", {"center": v(-29.8, 23.73) * mm, "radius": 25.4 * mm, "construction": true});
            skCircle(sketch, "E93", {"center": v(0, 38.1) * mm, "radius": 25.4 * mm, "construction": true});
            skLineSegment(sketch, "E94", {"start": v(8.55, 1.21) * mm, "end": v(42.9, 28.62) * mm, "construction": true});
            skLineSegment(sketch, "E95", {"start": v(4.87, -5.6) * mm, "end": v(50.8, -16.08) * mm, "construction": true});
            skLineSegment(sketch, "E96", {"start": v(-0.82, -8.4) * mm, "end": v(18.35, -48.15) * mm, "construction": true});
            skLineSegment(sketch, "E97", {"start": v(-6.58, -3.57) * mm, "end": v(-25.79, -43.52) * mm, "construction": true});
            skLineSegment(sketch, "E98", {"start": v(-6.3, 3.05) * mm, "end": v(-53.1, -7.67) * mm, "construction": true});
            skLineSegment(sketch, "E99", {"start": v(-2.27, 7.44) * mm, "end": v(-37.56, 35.54) * mm, "construction": true});
            skLineSegment(sketch, "E100", {"start": v(39.84, 26.17) * mm, "end": v(21.3, 11.39) * mm});
            skLineSegment(sketch, "E101", {"start": v(45.3, -14.82) * mm, "end": v(22.2, -9.55) * mm});
            skLineSegment(sketch, "E102", {"start": v(-24.52, -40.88) * mm, "end": v(-14.25, -19.51) * mm});
            skLineSegment(sketch, "E103", {"start": v(-14.25, -19.51) * mm, "end": v(-14.9, -20.08) * mm});
            skLineSegment(sketch, "E104", {"start": v(-47.24, -6.32) * mm, "end": v(-24.14, -1.03) * mm});
            skLineSegment(sketch, "E105", {"start": v(-24.14, -1.03) * mm, "end": v(-23.21, -0.35) * mm});
            skLineSegment(sketch, "E106", {"start": v(-34.39, 33) * mm, "end": v(-14.25, 16.98) * mm});
            skArc(sketch, "E107", {"start": v(-14.25, 16.98) * mm, "mid": v(-7.54, 13.47) * mm, "end": v(0, 12.7) * mm});
            skArc(sketch, "E108", {"start": v(21.3, 11.39) * mm, "mid": v(15.64, 5.04) * mm, "end": v(12.38, -2.82) * mm});
            skArc(sketch, "E109", {"start": v(22.2, -9.55) * mm, "mid": v(13.7, -9.08) * mm, "end": v(5.52, -11.44) * mm});
            skArc(sketch, "E110", {"start": v(-14.25, -19.51) * mm, "mid": v(-11.9, -11.33) * mm, "end": v(-12.38, -2.84) * mm});
            skArc(sketch, "E111", {"start": v(-24.14, -1.03) * mm, "mid": v(-16.28, 2.23) * mm, "end": v(-9.94, 7.9) * mm});
            skLineSegment(sketch, "E112", {"start": v(16.66, -44.66) * mm, "end": v(6.37, -23.3) * mm});
            skLineSegment(sketch, "E113", {"start": v(6.37, -23.3) * mm, "end": v(5.87, -22.75) * mm});
            skArc(sketch, "E114", {"start": v(6.37, -23.3) * mm, "mid": v(1.44, -16.37) * mm, "end": v(-5.5, -11.45) * mm});
            skLineSegment(sketch, "E115", {"start": v(12.38, -2.82) * mm, "end": v(4.34, -0.99) * mm});
            skLineSegment(sketch, "E116", {"start": v(4.34, -0.99) * mm, "end": v(38.7, 27.83) * mm});
            skLineSegment(sketch, "E117", {"start": v(38.7, 27.83) * mm, "end": v(39.84, 26.17) * mm});
            skLineSegment(sketch, "E118", {"start": v(5.52, -11.44) * mm, "end": v(1.36, -2.82) * mm});
            skLineSegment(sketch, "E119", {"start": v(1.36, -2.82) * mm, "end": v(45.87, -12.97) * mm});
            skLineSegment(sketch, "E120", {"start": v(45.87, -12.97) * mm, "end": v(45.3, -14.82) * mm});
            skLineSegment(sketch, "E121", {"start": v(-5.5, -11.45) * mm, "end": v(-1.99, -4.13) * mm});
            skLineSegment(sketch, "E122", {"start": v(-1.99, -4.13) * mm, "end": v(18.98, -43.72) * mm});
            skLineSegment(sketch, "E123", {"start": v(18.98, -43.72) * mm, "end": v(16.66, -44.66) * mm});
            skLineSegment(sketch, "E124", {"start": v(-12.38, -2.84) * mm, "end": v(-5.5, -1.26) * mm});
            skLineSegment(sketch, "E125", {"start": v(-5.5, -1.26) * mm, "end": v(-22.11, -42.23) * mm});
            skLineSegment(sketch, "E126", {"start": v(-22.11, -42.23) * mm, "end": v(-24.52, -40.88) * mm});
            skLineSegment(sketch, "E127", {"start": v(-9.94, 7.9) * mm, "end": v(-3.58, 5.34) * mm});
            skLineSegment(sketch, "E128", {"start": v(-3.58, 5.34) * mm, "end": v(-4.8, 0) * mm});
            skLineSegment(sketch, "E129", {"start": v(-4.8, 0) * mm, "end": v(-46.69, -9.6) * mm});
            skLineSegment(sketch, "E130", {"start": v(-46.69, -9.6) * mm, "end": v(-47.24, -6.32) * mm});
            skLineSegment(sketch, "E131", {"start": v(0, 12.7) * mm, "end": v(0, 5.44) * mm});
            skLineSegment(sketch, "E132", {"start": v(0, 5.44) * mm, "end": v(-35.96, 31.28) * mm});
            skLineSegment(sketch, "E133", {"start": v(-35.96, 31.28) * mm, "end": v(-34.39, 33) * mm});
            skCircle(sketch, "E134", {"center": v(0, 0) * mm, "radius": 53.98 * mm, "construction": true});
            skSolve(sketch);
        }
        {
            var Q0;
            Q0=makeQuery(id+"F6.imprint","IMPRINT",FACE,{"disambiguationData":[TD([[makeQuery(id+"F6.imprint","IMPRINT",EDGE,{"derivedFrom":sQuery(id+"F6.wireOp",EDGE,"E77")}),-1.0]])]});
            var Q1;
            Q1=makeQuery(id+"F6.imprint","IMPRINT",FACE,{"disambiguationData":[TD([[makeQuery(id+"F6.imprint","IMPRINT",EDGE,{"derivedFrom":sQuery(id+"F6.wireOp",EDGE,"E100")}),-1.0]])]});
            var Q2;
            Q2=makeQuery(id+"F6.imprint","IMPRINT",FACE,{"disambiguationData":[TD([[makeQuery(id+"F6.imprint","IMPRINT",EDGE,{"derivedFrom":sQuery(id+"F6.wireOp",EDGE,"E101")}),-1.0]])]});
            var Q3;
            Q3=makeQuery(id+"F6.imprint","IMPRINT",FACE,{"disambiguationData":[TD([[makeQuery(id+"F6.imprint","IMPRINT",EDGE,{"derivedFrom":sQuery(id+"F6.wireOp",EDGE,"E112")}),-1.0]])]});
            var Q4;
            Q4=makeQuery(id+"F6.imprint","IMPRINT",FACE,{"disambiguationData":[TD([[makeQuery(id+"F6.imprint","IMPRINT",EDGE,{"derivedFrom":sQuery(id+"F6.wireOp",EDGE,"E102")}),-1.0]])]});
            var Q5;
            Q5=makeQuery(id+"F6.imprint","IMPRINT",FACE,{"disambiguationData":[TD([[makeQuery(id+"F6.imprint","IMPRINT",EDGE,{"derivedFrom":sQuery(id+"F6.wireOp",EDGE,"E104")}),-1.0]])]});
            var Q6;
            Q6=makeQuery(id+"F6.imprint","IMPRINT",FACE,{"disambiguationData":[TD([[makeQuery(id+"F6.imprint","IMPRINT",EDGE,{"derivedFrom":sQuery(id+"F6.wireOp",EDGE,"E106")}),-1.0]])]});
            extrude(context, id + "F7", {"entities" : qUnion([Q0, Q1, Q2, Q3, Q4, Q5, Q6]), "operationType" : NewBodyOperationType.ADD, "depth" : 3.17 * mm, "offsetDistance" : 25.4 * mm});
        }
    });
